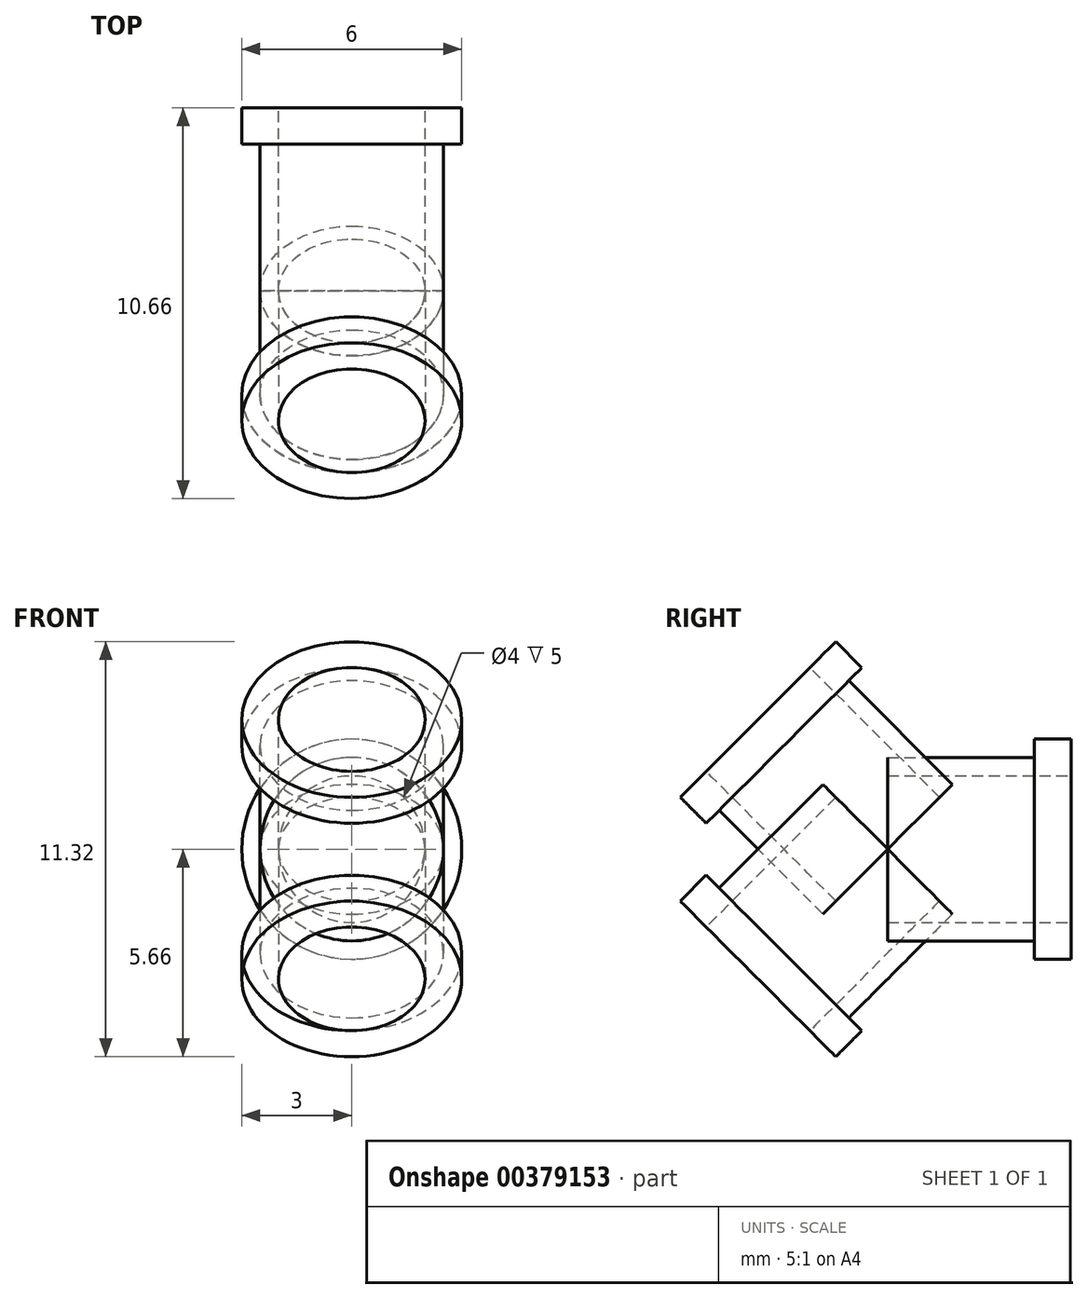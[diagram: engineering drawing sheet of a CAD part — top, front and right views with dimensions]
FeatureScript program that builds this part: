
annotation { "Feature Type Name" : "Feature", "Feature Type Description" : "" }
export const myFeature = defineFeature(function(context is Context, id is Id, definition is map)
    precondition{}
    {
        {
            var Q0;
            Q0=qCreatedBy(makeId("Top.planeOp"),FACE);
            var sketch = newSketch(context, id + "F0", { "sketchPlane" : qUnion([Q0])});
            skLineSegment(sketch, "E0", {"start": v(2, 0) * mm, "end": v(2, 5) * mm});
            skLineSegment(sketch, "E1", {"start": v(2, 5) * mm, "end": v(3, 5) * mm});
            skLineSegment(sketch, "E2", {"start": v(3, 5) * mm, "end": v(3, 4) * mm});
            skLineSegment(sketch, "E3", {"start": v(3, 4) * mm, "end": v(2.5, 4) * mm});
            skLineSegment(sketch, "E4", {"start": v(2.5, 4) * mm, "end": v(2.5, 0) * mm});
            skLineSegment(sketch, "E5", {"start": v(2.5, 0) * mm, "end": v(2, 0) * mm});
            skLineSegment(sketch, "E6", {"start": v(0, 9.45) * mm, "end": v(0, -0.8) * mm, "construction": true});
            skSolve(sketch);
        }
        {
            var Q0;
            Q0=makeQuery(id+"F0.imprint","IMPRINT",FACE,{"disambiguationData":[TD([[makeQuery(id+"F0.imprint","IMPRINT",EDGE,{"derivedFrom":sQuery(id+"F0.wireOp",EDGE,"E0")}),-1.0]])]});
            var Q1;
            Q1=sQuery(id+"F0.wireOp",EDGE,"E6");
            revolve(context, id + "F1", {"entities" : qUnion([Q0]), "axis" : qUnion([Q1]), "revolveType" : RevolveType.FULL});
        }
        {
            var Q0;
            Q0=qCreatedBy(makeId("Top.planeOp"),FACE);
            var sketch = newSketch(context, id + "F2", { "sketchPlane" : qUnion([Q0])});
            skLineSegment(sketch, "E7", {"start": v(29.2, 0) * mm, "end": v(-28.64, 0) * mm, "construction": true});
            skSolve(sketch);
        }
        {
            var Q0;
            Q0=makeQuery(id+"F1.opRevolve","SWEPT_BODY",BODY,{"disambiguationData":[OSD([sQuery(id+"F0.wireOp",EDGE,"E0"),sQuery(id+"F0.wireOp",EDGE,"E1"),sQuery(id+"F0.wireOp",EDGE,"E2"),sQuery(id+"F0.wireOp",EDGE,"E3"),sQuery(id+"F0.wireOp",EDGE,"E4"),sQuery(id+"F0.wireOp",EDGE,"E5")])]});
            var Q1;
            Q1=sQuery(id+"F2.wireOp",EDGE,"E7");
            transform(context, id + "F3", {"entities" : qUnion([Q0]), "transformType" : TransformType.ROTATION, "transformAxis" : qUnion([Q1]), "angle" : 135 * degree, "makeCopy" : true});
        }
        {
            var Q0;
            Q0=makeQuery(id+"F1.opRevolve","SWEPT_BODY",BODY,{"disambiguationData":[OSD([sQuery(id+"F0.wireOp",EDGE,"E0"),sQuery(id+"F0.wireOp",EDGE,"E1"),sQuery(id+"F0.wireOp",EDGE,"E2"),sQuery(id+"F0.wireOp",EDGE,"E3"),sQuery(id+"F0.wireOp",EDGE,"E4"),sQuery(id+"F0.wireOp",EDGE,"E5")])]});
            var Q1;
            Q1=sQuery(id+"F2.wireOp",EDGE,"E7");
            transform(context, id + "F4", {"entities" : qUnion([Q0]), "transformType" : TransformType.ROTATION, "transformAxis" : qUnion([Q1]), "angle" : 225 * degree, "makeCopy" : true});
        }
    });
